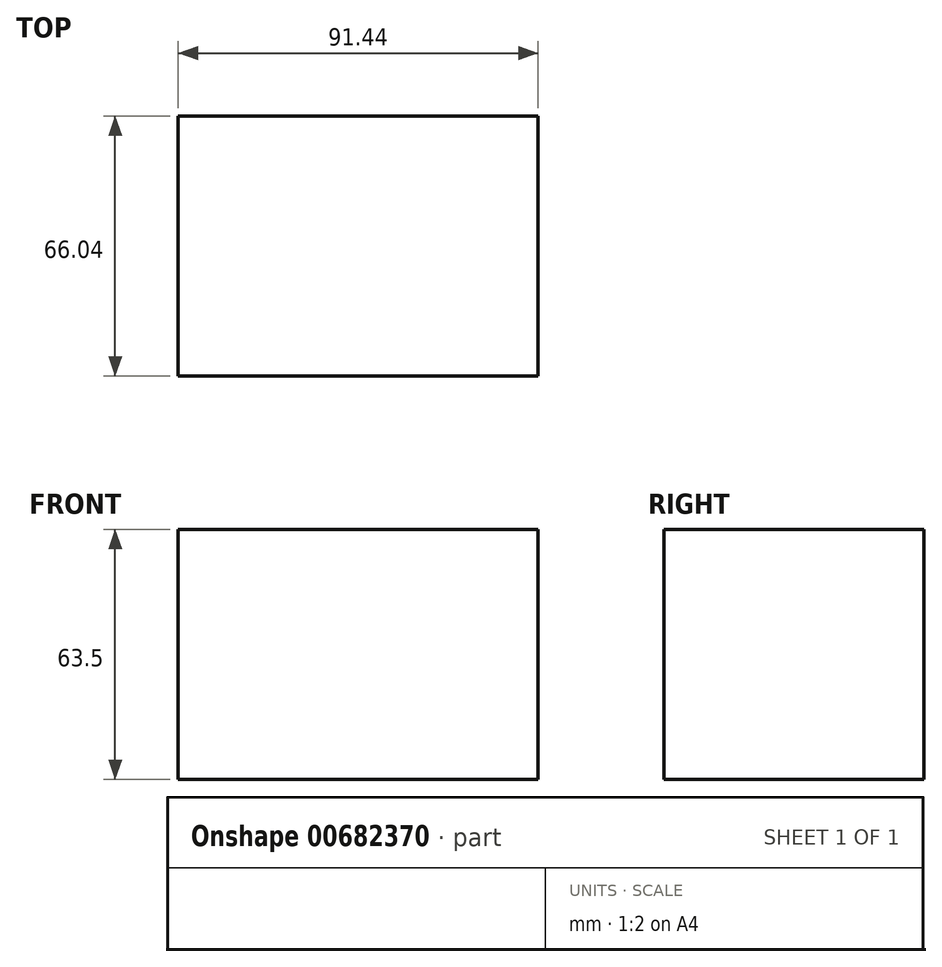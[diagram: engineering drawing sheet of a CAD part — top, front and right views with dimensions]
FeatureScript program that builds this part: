
annotation { "Feature Type Name" : "Feature", "Feature Type Description" : "" }
export const myFeature = defineFeature(function(context is Context, id is Id, definition is map)
    precondition{}
    {
        {
            var Q0;
            Q0=qCreatedBy(makeId("Top.planeOp"),FACE);
            var sketch = newSketch(context, id + "F0", { "sketchPlane" : qUnion([Q0])});
            skLineSegment(sketch, "E0.bottom", {"start": v(-31.08, 27.95) * mm, "end": v(60.36, 27.95) * mm});
            skLineSegment(sketch, "E0.top", {"start": v(-31.08, -38.1) * mm, "end": v(60.36, -38.1) * mm});
            skLineSegment(sketch, "E0.left", {"start": v(-31.08, 27.95) * mm, "end": v(-31.08, -38.1) * mm});
            skLineSegment(sketch, "E0.right", {"start": v(60.36, 27.95) * mm, "end": v(60.36, -38.1) * mm});
            skSolve(sketch);
        }
        {
            var Q0;
            Q0=makeQuery(id+"F0.imprint","IMPRINT",FACE,{"disambiguationData":[TD([[makeQuery(id+"F0.imprint","IMPRINT",EDGE,{"derivedFrom":sQuery(id+"F0.wireOp",EDGE,"E0.bottom")}),-1.0]])]});
            extrude(context, id + "F1", {"entities" : qUnion([Q0]), "depth" : 63.5 * mm, "offsetDistance" : 25.4 * mm});
        }
    });
